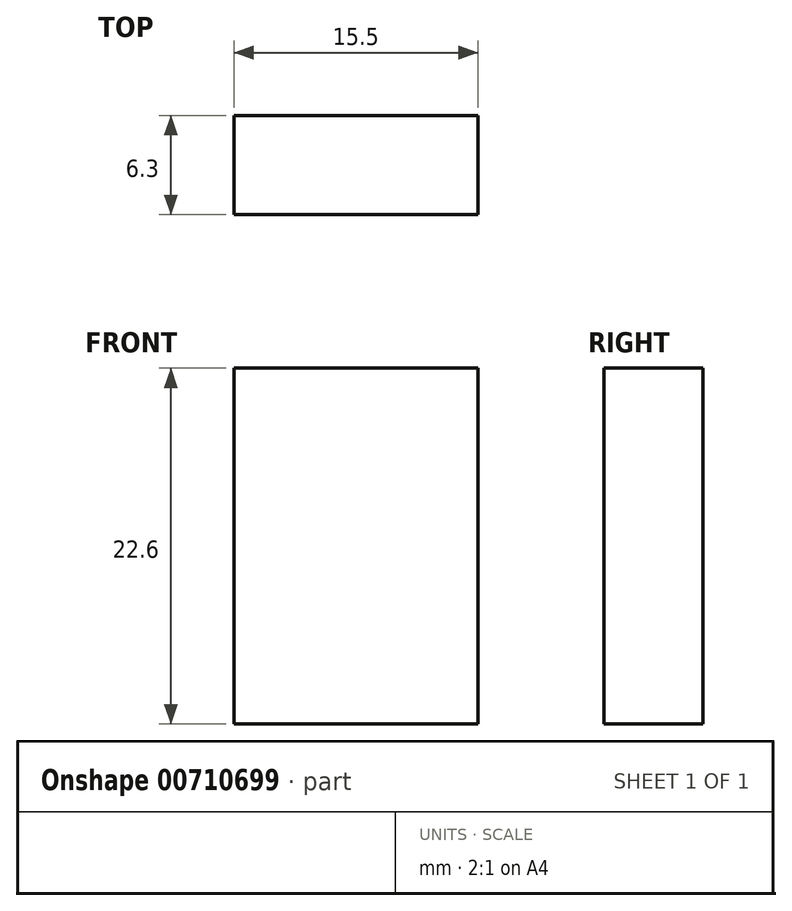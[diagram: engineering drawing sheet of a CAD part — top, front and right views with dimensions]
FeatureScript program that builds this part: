
annotation { "Feature Type Name" : "Feature", "Feature Type Description" : "" }
export const myFeature = defineFeature(function(context is Context, id is Id, definition is map)
    precondition{}
    {
        {
            var Q0;
            Q0=qCreatedBy(makeId("Top.planeOp"),FACE);
            var sketch = newSketch(context, id + "F0", { "sketchPlane" : qUnion([Q0])});
            skLineSegment(sketch, "E0.bottom", {"start": v(0, 0) * mm, "end": v(15.5, 0) * mm});
            skLineSegment(sketch, "E0.top", {"start": v(0, -6.3) * mm, "end": v(15.5, -6.3) * mm});
            skLineSegment(sketch, "E0.left", {"start": v(0, 0) * mm, "end": v(0, -6.3) * mm});
            skLineSegment(sketch, "E0.right", {"start": v(15.5, 0) * mm, "end": v(15.5, -6.3) * mm});
            skSolve(sketch);
        }
        {
            var Q0;
            Q0=makeQuery(id+"F0.imprint","IMPRINT",FACE,{"disambiguationData":[TD([[makeQuery(id+"F0.imprint","IMPRINT",EDGE,{"derivedFrom":sQuery(id+"F0.wireOp",EDGE,"E0.bottom")}),-1.0]])]});
            extrude(context, id + "F1", {"entities" : qUnion([Q0]), "depth" : 22.6 * mm, "offsetDistance" : 25 * mm});
        }
    });
